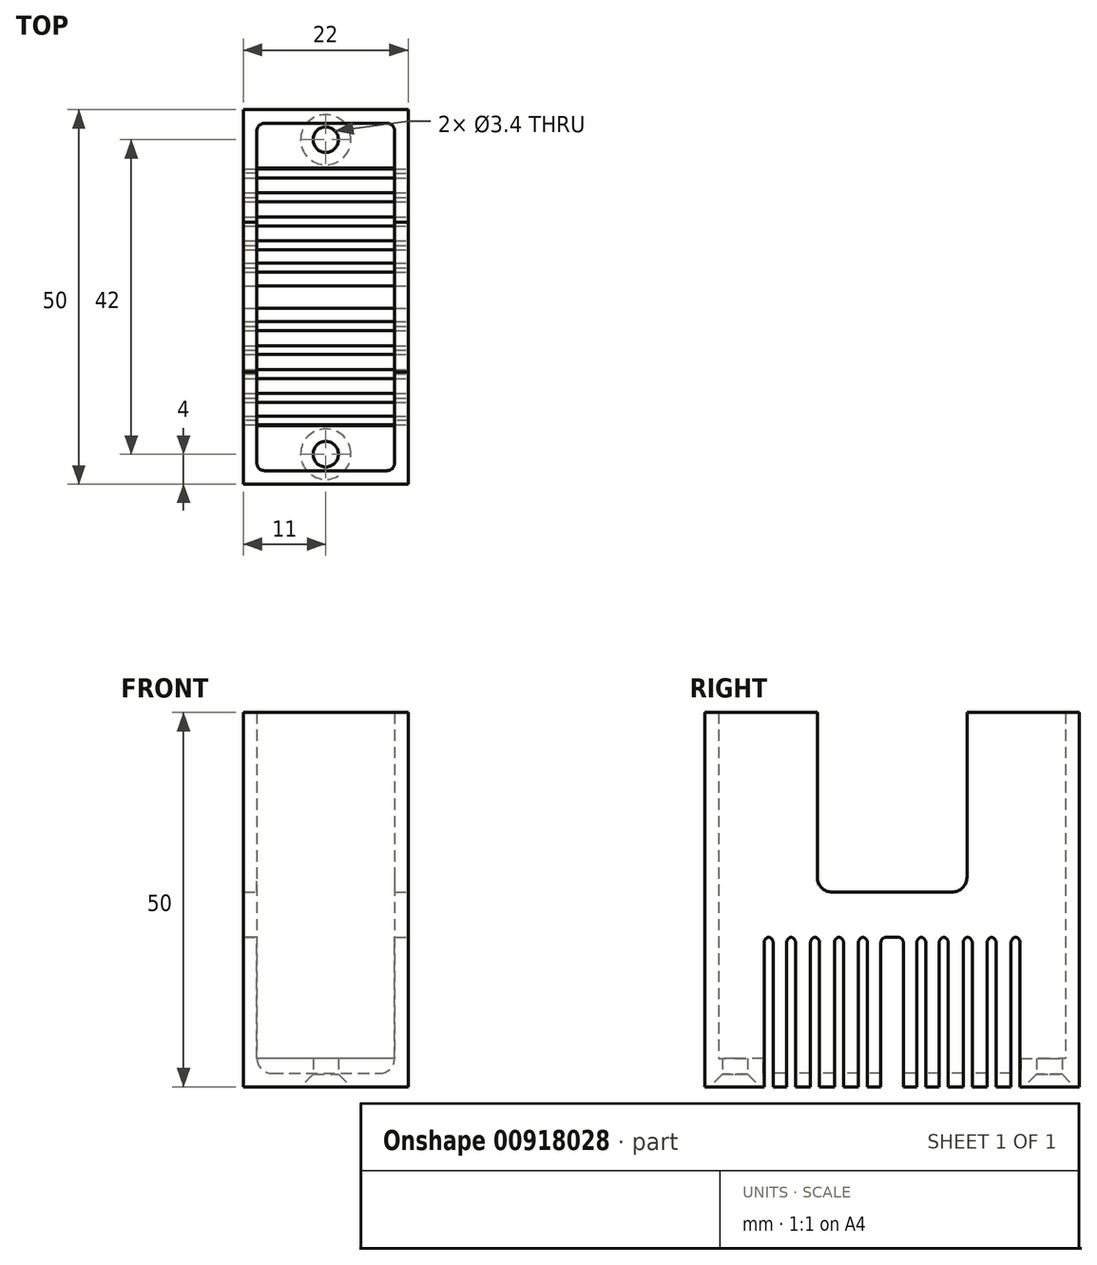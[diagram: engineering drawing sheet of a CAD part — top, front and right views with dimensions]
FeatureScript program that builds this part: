
annotation { "Feature Type Name" : "Feature", "Feature Type Description" : "" }
export const myFeature = defineFeature(function(context is Context, id is Id, definition is map)
    precondition{}
    {
        {
            var Q0;
            Q0=qCreatedBy(makeId("Top.planeOp"),FACE);
            var sketch = newSketch(context, id + "F0", { "sketchPlane" : qUnion([Q0])});
            skLineSegment(sketch, "E0.bottom", {"start": v(-11, 25) * mm, "end": v(11, 25) * mm});
            skLineSegment(sketch, "E0.top", {"start": v(-11, -25) * mm, "end": v(11, -25) * mm});
            skLineSegment(sketch, "E0.left", {"start": v(-11, 25) * mm, "end": v(-11, -25) * mm});
            skLineSegment(sketch, "E0.right", {"start": v(11, 25) * mm, "end": v(11, -25) * mm});
            skSolve(sketch);
        }
        {
            var Q0;
            Q0 = qSketchRegion(id + "F0", true);
            extrude(context, id + "F1", {"entities" : qUnion([Q0]), "depth" : 50 * mm, "offsetDistance" : 25 * mm});
        }
        {
            var Q0;
            Q0=makeQuery(id+"F1.opExtrude","CAP_FACE",FACE,{"disambiguationData":[OSD([sQuery(id+"F0.wireOp",EDGE,"E0.bottom"),sQuery(id+"F0.wireOp",EDGE,"E0.top"),sQuery(id+"F0.wireOp",EDGE,"E0.left"),sQuery(id+"F0.wireOp",EDGE,"E0.right")])],"isStart":false});
            shell(context, id + "F2", {"entities" : qUnion([Q0]), "thickness" : 1.8 * mm});
        }
        {
            var Q0;
            {var subQ0=sQuery(id+"F0.wireOp",EDGE,"E0.right");Q0=makeQuery(id+"F2.opShell","OFFSET_EDGE",EDGE,{"disambiguationData":[OSD([subQ0]),TDD([makeQuery(id+"F1.opExtrude","CAP_EDGE",EDGE,{"disambiguationData":[OSD([subQ0])],"isStart":true})])]});}
            var Q1;
            {var subQ0=sQuery(id+"F0.wireOp",EDGE,"E0.left");Q1=makeQuery(id+"F2.opShell","OFFSET_EDGE",EDGE,{"disambiguationData":[OSD([subQ0]),TDD([makeQuery(id+"F1.opExtrude","CAP_EDGE",EDGE,{"disambiguationData":[OSD([subQ0])],"isStart":true})])]});}
            fillet(context, id + "F3", {"entities" : qUnion([Q0, Q1]), "radius" : 2 * mm, "tangentPropagation" : true, "allowEdgeOverflow" : false});
        }
        {
            var Q0;
            Q0=makeQuery(id+"F1.opExtrude","CAP_FACE",FACE,{"disambiguationData":[OSD([sQuery(id+"F0.wireOp",EDGE,"E0.bottom"),sQuery(id+"F0.wireOp",EDGE,"E0.top"),sQuery(id+"F0.wireOp",EDGE,"E0.left"),sQuery(id+"F0.wireOp",EDGE,"E0.right")])],"isStart":true});
            var sketch = newSketch(context, id + "F4", { "sketchPlane" : qUnion([Q0])});
            skLineSegment(sketch, "E1.bottom", {"start": v(-16.27, 1.5) * mm, "end": v(17.28, 1.5) * mm});
            skLineSegment(sketch, "E1.top", {"start": v(-16.27, -1.5) * mm, "end": v(17.28, -1.5) * mm});
            skLineSegment(sketch, "E1.left", {"start": v(-16.27, 1.5) * mm, "end": v(-16.27, -1.5) * mm});
            skLineSegment(sketch, "E1.right", {"start": v(17.28, 1.5) * mm, "end": v(17.28, -1.5) * mm});
            skLineSegment(sketch, "E2.bottom", {"start": v(-15.07, 4.5) * mm, "end": v(15.13, 4.5) * mm});
            skLineSegment(sketch, "E2.top", {"start": v(-15.07, 3.3) * mm, "end": v(15.13, 3.3) * mm});
            skLineSegment(sketch, "E2.left", {"start": v(-15.07, 4.5) * mm, "end": v(-15.07, 3.3) * mm});
            skLineSegment(sketch, "E2.right", {"start": v(15.13, 4.5) * mm, "end": v(15.13, 3.3) * mm});
            skLineSegment(sketch, "E3.bottom", {"start": v(-13.5, 10.9) * mm, "end": v(12.58, 10.9) * mm});
            skLineSegment(sketch, "E3.top", {"start": v(-13.5, 9.7) * mm, "end": v(12.58, 9.7) * mm});
            skLineSegment(sketch, "E3.left", {"start": v(-13.5, 10.9) * mm, "end": v(-13.5, 9.7) * mm});
            skLineSegment(sketch, "E3.right", {"start": v(12.58, 10.9) * mm, "end": v(12.58, 9.7) * mm});
            skLineSegment(sketch, "E4.bottom", {"start": v(-13.9, -6.3) * mm, "end": v(11.6, -6.3) * mm});
            skLineSegment(sketch, "E4.top", {"start": v(-13.9, -7.5) * mm, "end": v(11.6, -7.5) * mm});
            skLineSegment(sketch, "E4.left", {"start": v(-13.9, -6.3) * mm, "end": v(-13.9, -7.5) * mm});
            skLineSegment(sketch, "E4.right", {"start": v(11.6, -6.3) * mm, "end": v(11.6, -7.5) * mm});
            skLineSegment(sketch, "E5.bottom", {"start": v(-14.1, -9.5) * mm, "end": v(12.78, -9.5) * mm});
            skLineSegment(sketch, "E5.top", {"start": v(-14.1, -10.7) * mm, "end": v(12.78, -10.7) * mm});
            skLineSegment(sketch, "E5.left", {"start": v(-14.1, -9.5) * mm, "end": v(-14.1, -10.7) * mm});
            skLineSegment(sketch, "E5.right", {"start": v(12.78, -9.5) * mm, "end": v(12.78, -10.7) * mm});
            skLineSegment(sketch, "E6.bottom", {"start": v(-13.4, -3.3) * mm, "end": v(12.2, -3.3) * mm});
            skLineSegment(sketch, "E6.top", {"start": v(-13.4, -4.5) * mm, "end": v(12.2, -4.5) * mm});
            skLineSegment(sketch, "E6.left", {"start": v(-13.4, -3.3) * mm, "end": v(-13.4, -4.5) * mm});
            skLineSegment(sketch, "E6.right", {"start": v(12.2, -3.3) * mm, "end": v(12.2, -4.5) * mm});
            skLineSegment(sketch, "E7.bottom", {"start": v(-11.84, 7.7) * mm, "end": v(11.4, 7.7) * mm});
            skLineSegment(sketch, "E7.top", {"start": v(-11.84, 6.5) * mm, "end": v(11.4, 6.5) * mm});
            skLineSegment(sketch, "E7.left", {"start": v(-11.84, 7.7) * mm, "end": v(-11.84, 6.5) * mm});
            skLineSegment(sketch, "E7.right", {"start": v(11.4, 7.7) * mm, "end": v(11.4, 6.5) * mm});
            skLineSegment(sketch, "E8.bottom", {"start": v(-15.5, 14.1) * mm, "end": v(15.65, 14.1) * mm});
            skLineSegment(sketch, "E8.top", {"start": v(-15.5, 12.9) * mm, "end": v(15.65, 12.9) * mm});
            skLineSegment(sketch, "E8.left", {"start": v(-15.5, 14.1) * mm, "end": v(-15.5, 12.9) * mm});
            skLineSegment(sketch, "E8.right", {"start": v(15.65, 14.1) * mm, "end": v(15.65, 12.9) * mm});
            skLineSegment(sketch, "E9.bottom", {"start": v(-17.44, -12.7) * mm, "end": v(19.43, -12.7) * mm});
            skLineSegment(sketch, "E9.top", {"start": v(-17.44, -13.9) * mm, "end": v(19.43, -13.9) * mm});
            skLineSegment(sketch, "E9.left", {"start": v(-17.44, -12.7) * mm, "end": v(-17.44, -13.9) * mm});
            skLineSegment(sketch, "E9.right", {"start": v(19.43, -12.7) * mm, "end": v(19.43, -13.9) * mm});
            skLineSegment(sketch, "E10.bottom", {"start": v(-14.63, 17.1) * mm, "end": v(15.65, 17.1) * mm});
            skLineSegment(sketch, "E10.top", {"start": v(-14.63, 15.9) * mm, "end": v(15.65, 15.9) * mm});
            skLineSegment(sketch, "E10.left", {"start": v(-14.63, 17.1) * mm, "end": v(-14.63, 15.9) * mm});
            skLineSegment(sketch, "E10.right", {"start": v(15.65, 17.1) * mm, "end": v(15.65, 15.9) * mm});
            skLineSegment(sketch, "E11.bottom", {"start": v(-14.4, -15.9) * mm, "end": v(17.22, -15.9) * mm});
            skLineSegment(sketch, "E11.top", {"start": v(-14.4, -17.1) * mm, "end": v(17.22, -17.1) * mm});
            skLineSegment(sketch, "E11.left", {"start": v(-14.4, -15.9) * mm, "end": v(-14.4, -17.1) * mm});
            skLineSegment(sketch, "E11.right", {"start": v(17.22, -15.9) * mm, "end": v(17.22, -17.1) * mm});
            skSolve(sketch);
        }
        {
            var Q0;
            Q0 = qSketchRegion(id + "F4", true);
            extrude(context, id + "F5", {"entities" : qUnion([Q0]), "operationType" : NewBodyOperationType.REMOVE, "oppositeDirection" : true, "depth" : 20 * mm, "offsetDistance" : 25 * mm});
        }
        {
            var Q0;
            {var subQ0=sQuery(id+"F0.wireOp",EDGE,"E0.bottom");var subQ1=sQuery(id+"F0.wireOp",EDGE,"E0.left");var subQ2=sQuery(id+"F0.wireOp",EDGE,"E0.right");Q0=makeQuery(id+"F5.boolean.opBoolean","SPLIT",FACE,{"disambiguationData":[TD([makeQuery(id+"F2.opShell","OFFSET_FACE",FACE,{"disambiguationData":[OSD([subQ0])]})])],"derivedFrom":makeQuery(id+"F2.opShell","OFFSET_FACE",FACE,{"disambiguationData":[OSD([subQ0,sQuery(id+"F0.wireOp",EDGE,"E0.top"),subQ1,subQ2])]})});}
            var sketch = newSketch(context, id + "F6", { "sketchPlane" : qUnion([Q0])});
            skLineSegment(sketch, "E12.bottom", {"start": v(10.34, 17.2) * mm, "end": v(-10.09, 17.2) * mm});
            skLineSegment(sketch, "E12.top", {"start": v(10.34, 23.2) * mm, "end": v(-10.09, 23.2) * mm});
            skLineSegment(sketch, "E12.left", {"start": v(10.34, 17.2) * mm, "end": v(10.34, 23.2) * mm});
            skLineSegment(sketch, "E12.right", {"start": v(-10.09, 17.2) * mm, "end": v(-10.09, 23.2) * mm});
            skSolve(sketch);
        }
        {
            var Q0;
            Q0 = qSketchRegion(id + "F6", true);
            extrude(context, id + "F7", {"entities" : qUnion([Q0]), "operationType" : NewBodyOperationType.ADD, "depth" : 2 * mm, "offsetDistance" : 25 * mm});
        }
        {
            var Q0;
            {var subQ0=sQuery(id+"F0.wireOp",EDGE,"E0.top");var subQ1=sQuery(id+"F0.wireOp",EDGE,"E0.left");var subQ2=sQuery(id+"F0.wireOp",EDGE,"E0.right");Q0=makeQuery(id+"F5.boolean.opBoolean","SPLIT",FACE,{"disambiguationData":[TD([makeQuery(id+"F2.opShell","OFFSET_FACE",FACE,{"disambiguationData":[OSD([subQ0])]})])],"derivedFrom":makeQuery(id+"F2.opShell","OFFSET_FACE",FACE,{"disambiguationData":[OSD([sQuery(id+"F0.wireOp",EDGE,"E0.bottom"),subQ0,subQ1,subQ2])]})});}
            var sketch = newSketch(context, id + "F8", { "sketchPlane" : qUnion([Q0])});
            skLineSegment(sketch, "E13.bottom", {"start": v(-10.35, -23.2) * mm, "end": v(10.18, -23.2) * mm});
            skLineSegment(sketch, "E13.top", {"start": v(-10.35, -17.2) * mm, "end": v(10.18, -17.2) * mm});
            skLineSegment(sketch, "E13.left", {"start": v(-10.35, -23.2) * mm, "end": v(-10.35, -17.2) * mm});
            skLineSegment(sketch, "E13.right", {"start": v(10.18, -23.2) * mm, "end": v(10.18, -17.2) * mm});
            skSolve(sketch);
        }
        {
            var Q0;
            Q0 = qSketchRegion(id + "F8", true);
            extrude(context, id + "F9", {"entities" : qUnion([Q0]), "operationType" : NewBodyOperationType.ADD, "depth" : 2 * mm, "offsetDistance" : 25 * mm});
        }
        {
            var Q0;
            Q0=makeQuery(id+"F2.opShell","OFFSET_EDGE",EDGE,{"disambiguationData":[OSD([sQuery(id+"F0.wireOp",EDGE,"E0.top"),sQuery(id+"F0.wireOp",EDGE,"E0.left")])]});
            var Q1;
            Q1=makeQuery(id+"F2.opShell","OFFSET_EDGE",EDGE,{"disambiguationData":[OSD([sQuery(id+"F0.wireOp",EDGE,"E0.top"),sQuery(id+"F0.wireOp",EDGE,"E0.right")])]});
            var Q2;
            Q2=makeQuery(id+"F2.opShell","OFFSET_EDGE",EDGE,{"disambiguationData":[OSD([sQuery(id+"F0.wireOp",EDGE,"E0.bottom"),sQuery(id+"F0.wireOp",EDGE,"E0.right")])]});
            var Q3;
            Q3=makeQuery(id+"F2.opShell","OFFSET_EDGE",EDGE,{"disambiguationData":[OSD([sQuery(id+"F0.wireOp",EDGE,"E0.bottom"),sQuery(id+"F0.wireOp",EDGE,"E0.left")])]});
            fillet(context, id + "F10", {"entities" : qUnion([Q0, Q1, Q2, Q3]), "radius" : 1 * mm, "tangentPropagation" : true, "allowEdgeOverflow" : false});
        }
        {
            var Q0;
            {var subQ0=sQuery(id+"F0.wireOp",EDGE,"E0.top");var subQ1=sQuery(id+"F0.wireOp",EDGE,"E0.left");var subQ2=sQuery(id+"F0.wireOp",EDGE,"E0.right");Q0=makeQuery(id+"F5.boolean.opBoolean","SPLIT",FACE,{"disambiguationData":[TD([makeQuery(id+"F1.opExtrude","SWEPT_FACE",FACE,{"disambiguationData":[OSD([subQ0])]})])],"derivedFrom":makeQuery(id+"F1.opExtrude","CAP_FACE",FACE,{"disambiguationData":[OSD([sQuery(id+"F0.wireOp",EDGE,"E0.bottom"),subQ0,subQ1,subQ2])],"isStart":true})});}
            var sketch = newSketch(context, id + "F11", { "sketchPlane" : qUnion([Q0])});
            skPoint(sketch, "E14", {"position": v(0, 21) * mm});
            skPoint(sketch, "E15", {"position": v(0, -21) * mm});
            skSolve(sketch);
        }
        {
            var Q0;
            Q0=sQuery(id+"F11.wireOp",VERTEX,"E14");
            var Q1;
            Q1=sQuery(id+"F11.wireOp",VERTEX,"E15");
            var Q2;
            Q2=makeQuery(id+"F1.opExtrude","SWEPT_BODY",BODY,{"disambiguationData":[OSD([sQuery(id+"F0.wireOp",EDGE,"E0.bottom"),sQuery(id+"F0.wireOp",EDGE,"E0.top"),sQuery(id+"F0.wireOp",EDGE,"E0.left"),sQuery(id+"F0.wireOp",EDGE,"E0.right")])]});
            hole(context, id + "F12", {"style" : HoleStyle.C_SINK, "endStyle" : HoleEndStyle.THROUGH, "standardTappedOrClearance" : lookupTablePath({ "fit" : "Normal", "standard" : "ISO", "size" : "M3", "type" : "Clearance" }), "standardBlindInLast" : lookupTablePath({ "fit" : "Normal", "standard" : "ISO", "engagement" : "75%", "pitch" : "0.5 mm", "size" : "M3", "type" : "Clearance & tapped" }), "holeDiameter" : 3.4 * mm, "cSinkDiameter" : 6.72 * mm, "cSinkAngle" : 90 * degree, "majorDiameter" : 5 * mm, "isTappedThrough" : true, "tappedDepth" : 12 * mm, "tapClearance" : 3, "locations" : qUnion([Q0, Q1]), "scope" : qUnion([Q2])});
        }
        {
            var Q0;
            {var subQ0=sQuery(id+"F0.wireOp",EDGE,"E0.left");var subQ1=sQuery(id+"F4.wireOp",EDGE,"E1.bottom");Q0=makeQuery(id+"F5.boolean.opBoolean","COPY",EDGE,{"disambiguationData":[TD([makeQuery(id+"F1.opExtrude","SWEPT_FACE",FACE,{"disambiguationData":[OSD([subQ0])]})])],"derivedFrom":makeQuery(id+"F5.opExtrude","CAP_EDGE",EDGE,{"disambiguationData":[OSD([subQ1])],"isStart":false})});}
            var Q1;
            {var subQ0=sQuery(id+"F0.wireOp",EDGE,"E0.left");var subQ1=sQuery(id+"F4.wireOp",EDGE,"E1.top");Q1=makeQuery(id+"F5.boolean.opBoolean","COPY",EDGE,{"disambiguationData":[TD([makeQuery(id+"F1.opExtrude","SWEPT_FACE",FACE,{"disambiguationData":[OSD([subQ0])]})])],"derivedFrom":makeQuery(id+"F5.opExtrude","CAP_EDGE",EDGE,{"disambiguationData":[OSD([subQ1])],"isStart":false})});}
            var Q2;
            {var subQ0=sQuery(id+"F0.wireOp",EDGE,"E0.right");var subQ1=sQuery(id+"F4.wireOp",EDGE,"E1.top");Q2=makeQuery(id+"F5.boolean.opBoolean","COPY",EDGE,{"disambiguationData":[TD([makeQuery(id+"F1.opExtrude","SWEPT_FACE",FACE,{"disambiguationData":[OSD([subQ0])]})])],"derivedFrom":makeQuery(id+"F5.opExtrude","CAP_EDGE",EDGE,{"disambiguationData":[OSD([subQ1])],"isStart":false})});}
            var Q3;
            {var subQ0=sQuery(id+"F0.wireOp",EDGE,"E0.right");var subQ1=sQuery(id+"F4.wireOp",EDGE,"E1.bottom");Q3=makeQuery(id+"F5.boolean.opBoolean","COPY",EDGE,{"disambiguationData":[TD([makeQuery(id+"F1.opExtrude","SWEPT_FACE",FACE,{"disambiguationData":[OSD([subQ0])]})])],"derivedFrom":makeQuery(id+"F5.opExtrude","CAP_EDGE",EDGE,{"disambiguationData":[OSD([subQ1])],"isStart":false})});}
            var Q4;
            {var subQ0=sQuery(id+"F0.wireOp",EDGE,"E0.left");var subQ1=sQuery(id+"F4.wireOp",EDGE,"E9.top");Q4=makeQuery(id+"F5.boolean.opBoolean","COPY",EDGE,{"disambiguationData":[TD([makeQuery(id+"F1.opExtrude","SWEPT_FACE",FACE,{"disambiguationData":[OSD([subQ0])]})])],"derivedFrom":makeQuery(id+"F5.opExtrude","CAP_EDGE",EDGE,{"disambiguationData":[OSD([subQ1])],"isStart":false})});}
            var Q5;
            {var subQ0=sQuery(id+"F0.wireOp",EDGE,"E0.left");var subQ1=sQuery(id+"F4.wireOp",EDGE,"E9.bottom");Q5=makeQuery(id+"F5.boolean.opBoolean","COPY",EDGE,{"disambiguationData":[TD([makeQuery(id+"F1.opExtrude","SWEPT_FACE",FACE,{"disambiguationData":[OSD([subQ0])]})])],"derivedFrom":makeQuery(id+"F5.opExtrude","CAP_EDGE",EDGE,{"disambiguationData":[OSD([subQ1])],"isStart":false})});}
            var Q6;
            {var subQ0=sQuery(id+"F0.wireOp",EDGE,"E0.left");var subQ1=sQuery(id+"F4.wireOp",EDGE,"E5.top");Q6=makeQuery(id+"F5.boolean.opBoolean","COPY",EDGE,{"disambiguationData":[TD([makeQuery(id+"F1.opExtrude","SWEPT_FACE",FACE,{"disambiguationData":[OSD([subQ0])]})])],"derivedFrom":makeQuery(id+"F5.opExtrude","CAP_EDGE",EDGE,{"disambiguationData":[OSD([subQ1])],"isStart":false})});}
            var Q7;
            {var subQ0=sQuery(id+"F0.wireOp",EDGE,"E0.left");var subQ1=sQuery(id+"F4.wireOp",EDGE,"E5.bottom");Q7=makeQuery(id+"F5.boolean.opBoolean","COPY",EDGE,{"disambiguationData":[TD([makeQuery(id+"F1.opExtrude","SWEPT_FACE",FACE,{"disambiguationData":[OSD([subQ0])]})])],"derivedFrom":makeQuery(id+"F5.opExtrude","CAP_EDGE",EDGE,{"disambiguationData":[OSD([subQ1])],"isStart":false})});}
            var Q8;
            {var subQ0=sQuery(id+"F0.wireOp",EDGE,"E0.left");var subQ1=sQuery(id+"F4.wireOp",EDGE,"E4.top");Q8=makeQuery(id+"F5.boolean.opBoolean","COPY",EDGE,{"disambiguationData":[TD([makeQuery(id+"F1.opExtrude","SWEPT_FACE",FACE,{"disambiguationData":[OSD([subQ0])]})])],"derivedFrom":makeQuery(id+"F5.opExtrude","CAP_EDGE",EDGE,{"disambiguationData":[OSD([subQ1])],"isStart":false})});}
            var Q9;
            {var subQ0=sQuery(id+"F0.wireOp",EDGE,"E0.left");var subQ1=sQuery(id+"F4.wireOp",EDGE,"E4.bottom");Q9=makeQuery(id+"F5.boolean.opBoolean","COPY",EDGE,{"disambiguationData":[TD([makeQuery(id+"F1.opExtrude","SWEPT_FACE",FACE,{"disambiguationData":[OSD([subQ0])]})])],"derivedFrom":makeQuery(id+"F5.opExtrude","CAP_EDGE",EDGE,{"disambiguationData":[OSD([subQ1])],"isStart":false})});}
            var Q10;
            {var subQ0=sQuery(id+"F0.wireOp",EDGE,"E0.left");var subQ1=sQuery(id+"F4.wireOp",EDGE,"E6.top");Q10=makeQuery(id+"F5.boolean.opBoolean","COPY",EDGE,{"disambiguationData":[TD([makeQuery(id+"F1.opExtrude","SWEPT_FACE",FACE,{"disambiguationData":[OSD([subQ0])]})])],"derivedFrom":makeQuery(id+"F5.opExtrude","CAP_EDGE",EDGE,{"disambiguationData":[OSD([subQ1])],"isStart":false})});}
            var Q11;
            {var subQ0=sQuery(id+"F0.wireOp",EDGE,"E0.left");var subQ1=sQuery(id+"F4.wireOp",EDGE,"E6.bottom");Q11=makeQuery(id+"F5.boolean.opBoolean","COPY",EDGE,{"disambiguationData":[TD([makeQuery(id+"F1.opExtrude","SWEPT_FACE",FACE,{"disambiguationData":[OSD([subQ0])]})])],"derivedFrom":makeQuery(id+"F5.opExtrude","CAP_EDGE",EDGE,{"disambiguationData":[OSD([subQ1])],"isStart":false})});}
            var Q12;
            {var subQ0=sQuery(id+"F0.wireOp",EDGE,"E0.left");var subQ1=sQuery(id+"F4.wireOp",EDGE,"E2.top");Q12=makeQuery(id+"F5.boolean.opBoolean","COPY",EDGE,{"disambiguationData":[TD([makeQuery(id+"F1.opExtrude","SWEPT_FACE",FACE,{"disambiguationData":[OSD([subQ0])]})])],"derivedFrom":makeQuery(id+"F5.opExtrude","CAP_EDGE",EDGE,{"disambiguationData":[OSD([subQ1])],"isStart":false})});}
            var Q13;
            {var subQ0=sQuery(id+"F0.wireOp",EDGE,"E0.left");var subQ1=sQuery(id+"F4.wireOp",EDGE,"E7.top");Q13=makeQuery(id+"F5.boolean.opBoolean","COPY",EDGE,{"disambiguationData":[TD([makeQuery(id+"F1.opExtrude","SWEPT_FACE",FACE,{"disambiguationData":[OSD([subQ0])]})])],"derivedFrom":makeQuery(id+"F5.opExtrude","CAP_EDGE",EDGE,{"disambiguationData":[OSD([subQ1])],"isStart":false})});}
            var Q14;
            {var subQ0=sQuery(id+"F0.wireOp",EDGE,"E0.left");var subQ1=sQuery(id+"F4.wireOp",EDGE,"E3.top");Q14=makeQuery(id+"F5.boolean.opBoolean","COPY",EDGE,{"disambiguationData":[TD([makeQuery(id+"F1.opExtrude","SWEPT_FACE",FACE,{"disambiguationData":[OSD([subQ0])]})])],"derivedFrom":makeQuery(id+"F5.opExtrude","CAP_EDGE",EDGE,{"disambiguationData":[OSD([subQ1])],"isStart":false})});}
            var Q15;
            {var subQ0=sQuery(id+"F0.wireOp",EDGE,"E0.left");var subQ1=sQuery(id+"F4.wireOp",EDGE,"E8.top");Q15=makeQuery(id+"F5.boolean.opBoolean","COPY",EDGE,{"disambiguationData":[TD([makeQuery(id+"F1.opExtrude","SWEPT_FACE",FACE,{"disambiguationData":[OSD([subQ0])]})])],"derivedFrom":makeQuery(id+"F5.opExtrude","CAP_EDGE",EDGE,{"disambiguationData":[OSD([subQ1])],"isStart":false})});}
            var Q16;
            {var subQ0=sQuery(id+"F0.wireOp",EDGE,"E0.left");var subQ1=sQuery(id+"F4.wireOp",EDGE,"E8.bottom");Q16=makeQuery(id+"F5.boolean.opBoolean","COPY",EDGE,{"disambiguationData":[TD([makeQuery(id+"F1.opExtrude","SWEPT_FACE",FACE,{"disambiguationData":[OSD([subQ0])]})])],"derivedFrom":makeQuery(id+"F5.opExtrude","CAP_EDGE",EDGE,{"disambiguationData":[OSD([subQ1])],"isStart":false})});}
            var Q17;
            {var subQ0=sQuery(id+"F0.wireOp",EDGE,"E0.left");var subQ1=sQuery(id+"F4.wireOp",EDGE,"E3.bottom");Q17=makeQuery(id+"F5.boolean.opBoolean","COPY",EDGE,{"disambiguationData":[TD([makeQuery(id+"F1.opExtrude","SWEPT_FACE",FACE,{"disambiguationData":[OSD([subQ0])]})])],"derivedFrom":makeQuery(id+"F5.opExtrude","CAP_EDGE",EDGE,{"disambiguationData":[OSD([subQ1])],"isStart":false})});}
            var Q18;
            {var subQ0=sQuery(id+"F0.wireOp",EDGE,"E0.left");var subQ1=sQuery(id+"F4.wireOp",EDGE,"E7.bottom");Q18=makeQuery(id+"F5.boolean.opBoolean","COPY",EDGE,{"disambiguationData":[TD([makeQuery(id+"F1.opExtrude","SWEPT_FACE",FACE,{"disambiguationData":[OSD([subQ0])]})])],"derivedFrom":makeQuery(id+"F5.opExtrude","CAP_EDGE",EDGE,{"disambiguationData":[OSD([subQ1])],"isStart":false})});}
            var Q19;
            {var subQ0=sQuery(id+"F0.wireOp",EDGE,"E0.left");var subQ1=sQuery(id+"F4.wireOp",EDGE,"E2.bottom");Q19=makeQuery(id+"F5.boolean.opBoolean","COPY",EDGE,{"disambiguationData":[TD([makeQuery(id+"F1.opExtrude","SWEPT_FACE",FACE,{"disambiguationData":[OSD([subQ0])]})])],"derivedFrom":makeQuery(id+"F5.opExtrude","CAP_EDGE",EDGE,{"disambiguationData":[OSD([subQ1])],"isStart":false})});}
            var Q20;
            {var subQ0=sQuery(id+"F0.wireOp",EDGE,"E0.right");var subQ1=sQuery(id+"F4.wireOp",EDGE,"E8.top");Q20=makeQuery(id+"F5.boolean.opBoolean","COPY",EDGE,{"disambiguationData":[TD([makeQuery(id+"F1.opExtrude","SWEPT_FACE",FACE,{"disambiguationData":[OSD([subQ0])]})])],"derivedFrom":makeQuery(id+"F5.opExtrude","CAP_EDGE",EDGE,{"disambiguationData":[OSD([subQ1])],"isStart":false})});}
            var Q21;
            {var subQ0=sQuery(id+"F0.wireOp",EDGE,"E0.right");var subQ1=sQuery(id+"F4.wireOp",EDGE,"E3.top");Q21=makeQuery(id+"F5.boolean.opBoolean","COPY",EDGE,{"disambiguationData":[TD([makeQuery(id+"F1.opExtrude","SWEPT_FACE",FACE,{"disambiguationData":[OSD([subQ0])]})])],"derivedFrom":makeQuery(id+"F5.opExtrude","CAP_EDGE",EDGE,{"disambiguationData":[OSD([subQ1])],"isStart":false})});}
            var Q22;
            {var subQ0=sQuery(id+"F0.wireOp",EDGE,"E0.right");var subQ1=sQuery(id+"F4.wireOp",EDGE,"E7.top");Q22=makeQuery(id+"F5.boolean.opBoolean","COPY",EDGE,{"disambiguationData":[TD([makeQuery(id+"F1.opExtrude","SWEPT_FACE",FACE,{"disambiguationData":[OSD([subQ0])]})])],"derivedFrom":makeQuery(id+"F5.opExtrude","CAP_EDGE",EDGE,{"disambiguationData":[OSD([subQ1])],"isStart":false})});}
            var Q23;
            {var subQ0=sQuery(id+"F0.wireOp",EDGE,"E0.right");var subQ1=sQuery(id+"F4.wireOp",EDGE,"E2.top");Q23=makeQuery(id+"F5.boolean.opBoolean","COPY",EDGE,{"disambiguationData":[TD([makeQuery(id+"F1.opExtrude","SWEPT_FACE",FACE,{"disambiguationData":[OSD([subQ0])]})])],"derivedFrom":makeQuery(id+"F5.opExtrude","CAP_EDGE",EDGE,{"disambiguationData":[OSD([subQ1])],"isStart":false})});}
            var Q24;
            {var subQ0=sQuery(id+"F0.wireOp",EDGE,"E0.right");var subQ1=sQuery(id+"F4.wireOp",EDGE,"E6.top");Q24=makeQuery(id+"F5.boolean.opBoolean","COPY",EDGE,{"disambiguationData":[TD([makeQuery(id+"F1.opExtrude","SWEPT_FACE",FACE,{"disambiguationData":[OSD([subQ0])]})])],"derivedFrom":makeQuery(id+"F5.opExtrude","CAP_EDGE",EDGE,{"disambiguationData":[OSD([subQ1])],"isStart":false})});}
            var Q25;
            {var subQ0=sQuery(id+"F0.wireOp",EDGE,"E0.right");var subQ1=sQuery(id+"F4.wireOp",EDGE,"E4.top");Q25=makeQuery(id+"F5.boolean.opBoolean","COPY",EDGE,{"disambiguationData":[TD([makeQuery(id+"F1.opExtrude","SWEPT_FACE",FACE,{"disambiguationData":[OSD([subQ0])]})])],"derivedFrom":makeQuery(id+"F5.opExtrude","CAP_EDGE",EDGE,{"disambiguationData":[OSD([subQ1])],"isStart":false})});}
            var Q26;
            {var subQ0=sQuery(id+"F0.wireOp",EDGE,"E0.right");var subQ1=sQuery(id+"F4.wireOp",EDGE,"E5.top");Q26=makeQuery(id+"F5.boolean.opBoolean","COPY",EDGE,{"disambiguationData":[TD([makeQuery(id+"F1.opExtrude","SWEPT_FACE",FACE,{"disambiguationData":[OSD([subQ0])]})])],"derivedFrom":makeQuery(id+"F5.opExtrude","CAP_EDGE",EDGE,{"disambiguationData":[OSD([subQ1])],"isStart":false})});}
            var Q27;
            {var subQ0=sQuery(id+"F0.wireOp",EDGE,"E0.right");var subQ1=sQuery(id+"F4.wireOp",EDGE,"E9.top");Q27=makeQuery(id+"F5.boolean.opBoolean","COPY",EDGE,{"disambiguationData":[TD([makeQuery(id+"F1.opExtrude","SWEPT_FACE",FACE,{"disambiguationData":[OSD([subQ0])]})])],"derivedFrom":makeQuery(id+"F5.opExtrude","CAP_EDGE",EDGE,{"disambiguationData":[OSD([subQ1])],"isStart":false})});}
            var Q28;
            {var subQ0=sQuery(id+"F0.wireOp",EDGE,"E0.right");var subQ1=sQuery(id+"F4.wireOp",EDGE,"E8.bottom");Q28=makeQuery(id+"F5.boolean.opBoolean","COPY",EDGE,{"disambiguationData":[TD([makeQuery(id+"F1.opExtrude","SWEPT_FACE",FACE,{"disambiguationData":[OSD([subQ0])]})])],"derivedFrom":makeQuery(id+"F5.opExtrude","CAP_EDGE",EDGE,{"disambiguationData":[OSD([subQ1])],"isStart":false})});}
            var Q29;
            {var subQ0=sQuery(id+"F0.wireOp",EDGE,"E0.right");var subQ1=sQuery(id+"F4.wireOp",EDGE,"E3.bottom");Q29=makeQuery(id+"F5.boolean.opBoolean","COPY",EDGE,{"disambiguationData":[TD([makeQuery(id+"F1.opExtrude","SWEPT_FACE",FACE,{"disambiguationData":[OSD([subQ0])]})])],"derivedFrom":makeQuery(id+"F5.opExtrude","CAP_EDGE",EDGE,{"disambiguationData":[OSD([subQ1])],"isStart":false})});}
            var Q30;
            {var subQ0=sQuery(id+"F0.wireOp",EDGE,"E0.right");var subQ1=sQuery(id+"F4.wireOp",EDGE,"E7.bottom");Q30=makeQuery(id+"F5.boolean.opBoolean","COPY",EDGE,{"disambiguationData":[TD([makeQuery(id+"F1.opExtrude","SWEPT_FACE",FACE,{"disambiguationData":[OSD([subQ0])]})])],"derivedFrom":makeQuery(id+"F5.opExtrude","CAP_EDGE",EDGE,{"disambiguationData":[OSD([subQ1])],"isStart":false})});}
            var Q31;
            {var subQ0=sQuery(id+"F0.wireOp",EDGE,"E0.right");var subQ1=sQuery(id+"F4.wireOp",EDGE,"E2.bottom");Q31=makeQuery(id+"F5.boolean.opBoolean","COPY",EDGE,{"disambiguationData":[TD([makeQuery(id+"F1.opExtrude","SWEPT_FACE",FACE,{"disambiguationData":[OSD([subQ0])]})])],"derivedFrom":makeQuery(id+"F5.opExtrude","CAP_EDGE",EDGE,{"disambiguationData":[OSD([subQ1])],"isStart":false})});}
            var Q32;
            {var subQ0=sQuery(id+"F0.wireOp",EDGE,"E0.right");var subQ1=sQuery(id+"F4.wireOp",EDGE,"E6.bottom");Q32=makeQuery(id+"F5.boolean.opBoolean","COPY",EDGE,{"disambiguationData":[TD([makeQuery(id+"F1.opExtrude","SWEPT_FACE",FACE,{"disambiguationData":[OSD([subQ0])]})])],"derivedFrom":makeQuery(id+"F5.opExtrude","CAP_EDGE",EDGE,{"disambiguationData":[OSD([subQ1])],"isStart":false})});}
            var Q33;
            {var subQ0=sQuery(id+"F0.wireOp",EDGE,"E0.right");var subQ1=sQuery(id+"F4.wireOp",EDGE,"E4.bottom");Q33=makeQuery(id+"F5.boolean.opBoolean","COPY",EDGE,{"disambiguationData":[TD([makeQuery(id+"F1.opExtrude","SWEPT_FACE",FACE,{"disambiguationData":[OSD([subQ0])]})])],"derivedFrom":makeQuery(id+"F5.opExtrude","CAP_EDGE",EDGE,{"disambiguationData":[OSD([subQ1])],"isStart":false})});}
            var Q34;
            {var subQ0=sQuery(id+"F0.wireOp",EDGE,"E0.right");var subQ1=sQuery(id+"F4.wireOp",EDGE,"E5.bottom");Q34=makeQuery(id+"F5.boolean.opBoolean","COPY",EDGE,{"disambiguationData":[TD([makeQuery(id+"F1.opExtrude","SWEPT_FACE",FACE,{"disambiguationData":[OSD([subQ0])]})])],"derivedFrom":makeQuery(id+"F5.opExtrude","CAP_EDGE",EDGE,{"disambiguationData":[OSD([subQ1])],"isStart":false})});}
            var Q35;
            {var subQ0=sQuery(id+"F0.wireOp",EDGE,"E0.right");var subQ1=sQuery(id+"F4.wireOp",EDGE,"E9.bottom");Q35=makeQuery(id+"F5.boolean.opBoolean","COPY",EDGE,{"disambiguationData":[TD([makeQuery(id+"F1.opExtrude","SWEPT_FACE",FACE,{"disambiguationData":[OSD([subQ0])]})])],"derivedFrom":makeQuery(id+"F5.opExtrude","CAP_EDGE",EDGE,{"disambiguationData":[OSD([subQ1])],"isStart":false})});}
            var Q36;
            {var subQ0=sQuery(id+"F0.wireOp",EDGE,"E0.right");var subQ1=sQuery(id+"F4.wireOp",EDGE,"E10.bottom");Q36=makeQuery(id+"F5.boolean.opBoolean","COPY",EDGE,{"disambiguationData":[TD([makeQuery(id+"F1.opExtrude","SWEPT_FACE",FACE,{"disambiguationData":[OSD([subQ0])]})])],"derivedFrom":makeQuery(id+"F5.opExtrude","CAP_EDGE",EDGE,{"disambiguationData":[OSD([subQ1])],"isStart":false})});}
            var Q37;
            {var subQ0=sQuery(id+"F0.wireOp",EDGE,"E0.right");var subQ1=sQuery(id+"F4.wireOp",EDGE,"E10.top");Q37=makeQuery(id+"F5.boolean.opBoolean","COPY",EDGE,{"disambiguationData":[TD([makeQuery(id+"F1.opExtrude","SWEPT_FACE",FACE,{"disambiguationData":[OSD([subQ0])]})])],"derivedFrom":makeQuery(id+"F5.opExtrude","CAP_EDGE",EDGE,{"disambiguationData":[OSD([subQ1])],"isStart":false})});}
            var Q38;
            {var subQ0=sQuery(id+"F0.wireOp",EDGE,"E0.right");var subQ1=sQuery(id+"F4.wireOp",EDGE,"E11.top");Q38=makeQuery(id+"F5.boolean.opBoolean","COPY",EDGE,{"disambiguationData":[TD([makeQuery(id+"F1.opExtrude","SWEPT_FACE",FACE,{"disambiguationData":[OSD([subQ0])]})])],"derivedFrom":makeQuery(id+"F5.opExtrude","CAP_EDGE",EDGE,{"disambiguationData":[OSD([subQ1])],"isStart":false})});}
            var Q39;
            {var subQ0=sQuery(id+"F0.wireOp",EDGE,"E0.right");var subQ1=sQuery(id+"F4.wireOp",EDGE,"E11.bottom");Q39=makeQuery(id+"F5.boolean.opBoolean","COPY",EDGE,{"disambiguationData":[TD([makeQuery(id+"F1.opExtrude","SWEPT_FACE",FACE,{"disambiguationData":[OSD([subQ0])]})])],"derivedFrom":makeQuery(id+"F5.opExtrude","CAP_EDGE",EDGE,{"disambiguationData":[OSD([subQ1])],"isStart":false})});}
            var Q40;
            {var subQ0=sQuery(id+"F0.wireOp",EDGE,"E0.left");var subQ1=sQuery(id+"F4.wireOp",EDGE,"E11.bottom");Q40=makeQuery(id+"F5.boolean.opBoolean","COPY",EDGE,{"disambiguationData":[TD([makeQuery(id+"F1.opExtrude","SWEPT_FACE",FACE,{"disambiguationData":[OSD([subQ0])]})])],"derivedFrom":makeQuery(id+"F5.opExtrude","CAP_EDGE",EDGE,{"disambiguationData":[OSD([subQ1])],"isStart":false})});}
            var Q41;
            {var subQ0=sQuery(id+"F0.wireOp",EDGE,"E0.left");var subQ1=sQuery(id+"F4.wireOp",EDGE,"E11.top");Q41=makeQuery(id+"F5.boolean.opBoolean","COPY",EDGE,{"disambiguationData":[TD([makeQuery(id+"F1.opExtrude","SWEPT_FACE",FACE,{"disambiguationData":[OSD([subQ0])]})])],"derivedFrom":makeQuery(id+"F5.opExtrude","CAP_EDGE",EDGE,{"disambiguationData":[OSD([subQ1])],"isStart":false})});}
            var Q42;
            {var subQ0=sQuery(id+"F0.wireOp",EDGE,"E0.left");var subQ1=sQuery(id+"F4.wireOp",EDGE,"E10.bottom");Q42=makeQuery(id+"F5.boolean.opBoolean","COPY",EDGE,{"disambiguationData":[TD([makeQuery(id+"F1.opExtrude","SWEPT_FACE",FACE,{"disambiguationData":[OSD([subQ0])]})])],"derivedFrom":makeQuery(id+"F5.opExtrude","CAP_EDGE",EDGE,{"disambiguationData":[OSD([subQ1])],"isStart":false})});}
            var Q43;
            {var subQ0=sQuery(id+"F0.wireOp",EDGE,"E0.left");var subQ1=sQuery(id+"F4.wireOp",EDGE,"E10.top");Q43=makeQuery(id+"F5.boolean.opBoolean","COPY",EDGE,{"disambiguationData":[TD([makeQuery(id+"F1.opExtrude","SWEPT_FACE",FACE,{"disambiguationData":[OSD([subQ0])]})])],"derivedFrom":makeQuery(id+"F5.opExtrude","CAP_EDGE",EDGE,{"disambiguationData":[OSD([subQ1])],"isStart":false})});}
            fillet(context, id + "F13", {"entities" : qUnion([Q0, Q1, Q2, Q3, Q4, Q5, Q6, Q7, Q8, Q9, Q10, Q11, Q12, Q13, Q14, Q15, Q16, Q17, Q18, Q19, Q20, Q21, Q22, Q23, Q24, Q25, Q26, Q27, Q28, Q29, Q30, Q31, Q32, Q33, Q34, Q35, Q36, Q37, Q38, Q39, Q40, Q41, Q42, Q43]), "radius" : 0.75 * mm, "tangentPropagation" : true, "allowEdgeOverflow" : false});
        }
        {
            var Q0;
            Q0=makeQuery(id+"F1.opExtrude","SWEPT_FACE",FACE,{"disambiguationData":[OSD([sQuery(id+"F0.wireOp",EDGE,"E0.right")])]});
            var sketch = newSketch(context, id + "F14", { "sketchPlane" : qUnion([Q0])});
            skLineSegment(sketch, "E16.bottom", {"start": v(-10, 50) * mm, "end": v(10, 50) * mm});
            skLineSegment(sketch, "E16.top", {"start": v(-8, 26) * mm, "end": v(8, 26) * mm});
            skLineSegment(sketch, "E16.left", {"start": v(-10, 50) * mm, "end": v(-10, 28) * mm});
            skLineSegment(sketch, "E16.right", {"start": v(10, 50) * mm, "end": v(10, 28) * mm});
            skPoint(sketch, "E17.visualSharp", {"position": v(-10, 26) * mm});
            skArc(sketch, "E17.filletArc", {"start": v(-10, 28) * mm, "mid": v(-9.41, 26.59) * mm, "end": v(-8, 26) * mm});
            skPoint(sketch, "E18.visualSharp", {"position": v(10, 26) * mm});
            skArc(sketch, "E18.filletArc", {"start": v(8, 26) * mm, "mid": v(9.41, 26.59) * mm, "end": v(10, 28) * mm});
            skSolve(sketch);
        }
        {
            var Q0;
            Q0 = qSketchRegion(id + "F14", true);
            extrude(context, id + "F15", {"entities" : qUnion([Q0]), "operationType" : NewBodyOperationType.REMOVE, "endBound" : BoundingType.THROUGH_ALL, "oppositeDirection" : true, "depth" : 25 * mm, "offsetDistance" : 25 * mm});
        }
    });
